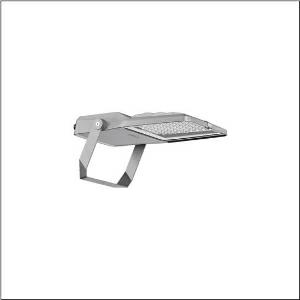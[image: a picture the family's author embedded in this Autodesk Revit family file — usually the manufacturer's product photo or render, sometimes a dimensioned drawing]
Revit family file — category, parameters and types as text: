
# Revit family: floodlight_fl_21_iq_mini___rs12_5xa7771d4b1a_77d6
name_source: partatom
category: Lighting Fixtures
units: mm (PartAtom-declared; Revit-internal decimal feet)

## family parameters
Cut with Voids When Loaded = No
Host = Face
Light Source = No
Part Type = Normal
Room Calculation Point = No
Round Connector Dimension = Use Diameter
Shared = No

## types (1)
- --- (1 x LED, 18810 lm, 143 W, 4000K)
    Apparent Load = 143 VA
    CIE Flux Codes = 79 92 99 100 100
    Color Rendering = 70
    Color Temperature = 4000K
    Default Elevation = 1800 mm
    Description = Floodlight FL 21 iQ mini, floodlight, primary light control with lens, of PMMA, primary optical cover: protective disc, of toughened safety glass, transparent, light distribution: RS12, light emission: direct distribution, installation type: surface-mounted, LED, High Power LED, rated luminous flux: 18.810lm, luminous efficacy: 132lm/W, light colour: 740, colour temperature: 4000K, control gear: iQ Comfort/DALI, control: Auto-Match, Temp-Guard, Lumen-Switch, Night-Set, Smart-Wire, Light-Fading, Desk-Remote (wireless, voltage-free reading and setting of iQ features in the workshop via application-optimized NFC function/RFID function), optimised constant luminous flux control (CLO 2.0), with terminal, 6-pole, mains connection: 220..240V, AC, 50/60Hz, start of lifetime: 143W, end of service life: 152W, reduction: 61W, luminaire housing, of diecast aluminium, powder-coated, Siteco® metallic grey (DB 702S), corrosivity category C5 mid according to DIN EN ISO 12944, suitable for swimming pools, chlorine-resistant, sealing non-destructively replaceable, mounting bracket, of steel, galvanised, powder-coated, Siteco® metallic grey (DB 702S), protection rating (complete): IP66, insulation class (complete): insulation class II (safety insulation), certification: CE, ENEC, VDE, protection symbol: D, impact resistance: IK08, permissible operating ambient temperature: -40..+40°C, permissible operating ambient temperature for outdoor applications: -40..+50°C, standard: DIN EN 12944, LABS conformity tested according to VDMA 24364:2018-05, packaging unit: 1 piece

Light Distribution: RS12
    Height = 70 mm
    Lamp = 1 x LED
    Lamp Light Flux = 18810 lm
    Lamp Power = 143 W
    Lamp count = 1
    Length = 485 mm
    Luminous efficacy = 132 lm/W
    Manufacturer = Siteco
    ModVariant = No
    Model = 5XA7771D4B1A
    Number of Poles = 1
    OnlyDefault = Yes
    Power Factor = 1
    Product Name = Floodlight FL 21 iQ mini | RS12
    Product group = floodlight | pylon annexe
    ProductGroupID = 6200
    Protection Class = Protection class II
    Protection Degree = IP 66
    RLX_Detail_Level = 1
    RLX_Emergency_Light_Flux = 0 lm
    RLX_Emergency_Type = 0
    RLX_Emergency_Type_DB = No
    RlxData = <blob elided: 91261 chars, md5=dc59f16a>
    Socket = socket
    Standby Power = 0 W
    System Light Flux = 18810 lm
    System Power = 143 W
    Type Comments = factory setting: luminous flux: 100 % | dim-lin: 254 | 730 mA
    Type Image = l_1006845.jpg
    URL = http://relux.com
    VarID = @adj_167452
    Voltage = 0 V
    Weight = 0.00 kg
    Width = 337 mm

## geometry (parser evidence)
native form markers: Blend x4, Sweep x13
no freeform markers — native parametric forms only
